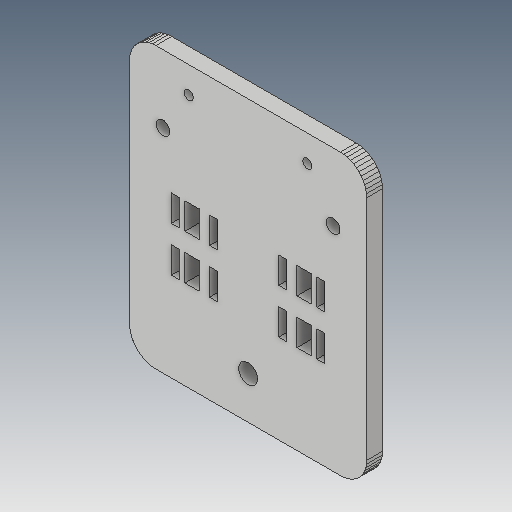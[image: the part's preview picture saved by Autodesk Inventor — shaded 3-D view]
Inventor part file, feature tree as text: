
AUTODESK INVENTOR PART (.ipt)
format: ipt  version: 2017 (Build 210142000, 142)  size: 313,856 bytes
history: native  units: mm
features: sketch x4, other x3
ambient origin geometry x8: Origin, YZ Plane, XZ Plane, XY Plane, X Axis, Y Axis, Z Axis, Center Point
bodies: Solid1 (feature_tree)
feature tree (7):
  other  "X-Axis-End-Plate.ipt"
  other  "Solid1::X-Axis-End-Plate.ipt"
  other  "TaggingFeature1"
  sketch  "Sketch1"  dims[d0=10.0mm]
  sketch  "Sketch2"
  sketch  "Sketch3"
  sketch  "Sketch4"
